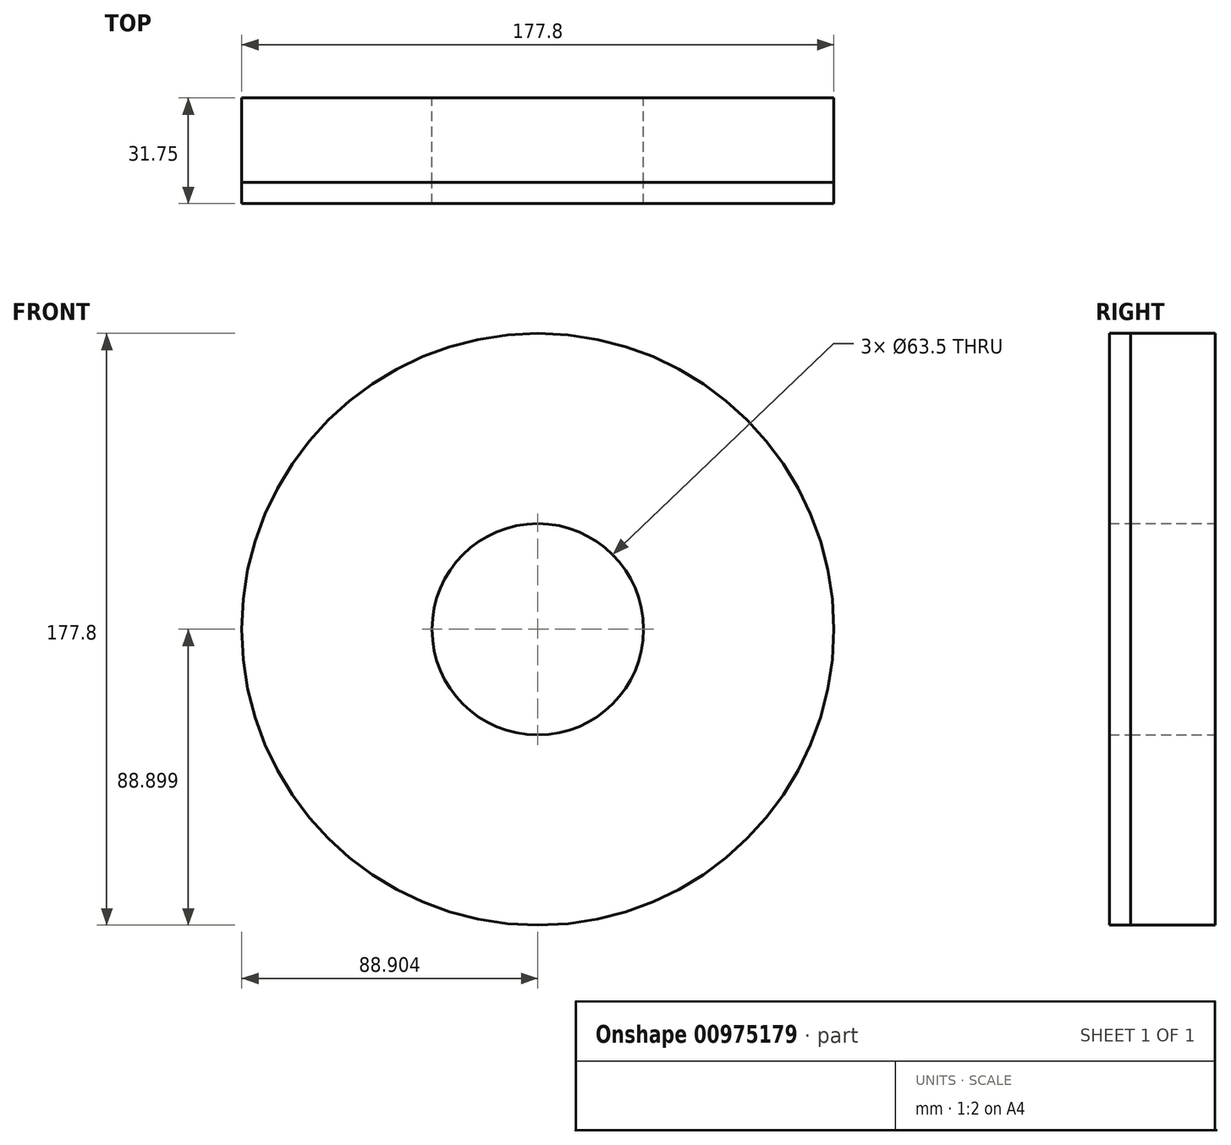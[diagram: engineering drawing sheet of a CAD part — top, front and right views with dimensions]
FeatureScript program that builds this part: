
annotation { "Feature Type Name" : "Feature", "Feature Type Description" : "" }
export const myFeature = defineFeature(function(context is Context, id is Id, definition is map)
    precondition{}
    {
        {
            var Q0;
            Q0=qCreatedBy(makeId("Front.planeOp"),FACE);
            var sketch = newSketch(context, id + "F0", { "sketchPlane" : qUnion([Q0])});
            skCircle(sketch, "E0", {"center": v(-91.18, 7.48) * mm, "radius": 88.9 * mm});
            skSolve(sketch);
        }
        {
            var Q0;
            Q0=makeQuery(id+"F0.imprint","IMPRINT",FACE,{"disambiguationData":[TD([[makeQuery(id+"F0.imprint","IMPRINT",EDGE,{"derivedFrom":sQuery(id+"F0.wireOp",EDGE,"E0")}),1.0]])]});
            extrude(context, id + "F1", {"entities" : qUnion([Q0]), "depth" : 6.35 * mm, "offsetDistance" : 25.4 * mm});
        }
        {
            var Q0;
            Q0=makeQuery(id+"F1.opExtrude","CAP_FACE",FACE,{"disambiguationData":[OSD([sQuery(id+"F0.wireOp",EDGE,"E0")])],"isStart":false});
            var sketch = newSketch(context, id + "F2", { "sketchPlane" : qUnion([Q0])});
            skLineSegment(sketch, "E1", {"start": v(-91.18, 96.38) * mm, "end": v(-91.18, -81.42) * mm});
            skCircle(sketch, "E2", {"center": v(-91.18, 7.48) * mm, "radius": 25.4 * mm});
            skCircle(sketch, "E3", {"center": v(-91.18, 7.48) * mm, "radius": 31.75 * mm});
            skSolve(sketch);
        }
        {
            var Q0;
            {var subQ0=sQuery(id+"F2.wireOp",EDGE,"E3");var subQ1=sQuery(id+"F2.wireOp",EDGE,"E1");var subQ2=makeQuery(id+"F2.imprint","INTERSECT",VERTEX,{"disambiguationData":[OD(0.0)],"derivedFrom":[subQ1,subQ0]});Q0=makeQuery(id+"F2.imprint","IMPRINT",FACE,{"disambiguationData":[TD([[makeQuery(id+"F2.imprint","IMPRINT",EDGE,{"disambiguationData":[TD([[subQ2,-1.0]])],"derivedFrom":subQ1}),-1.0]])]});}
            var Q1;
            {var subQ0=sQuery(id+"F2.wireOp",EDGE,"E3");var subQ1=sQuery(id+"F2.wireOp",EDGE,"E1");var subQ2=makeQuery(id+"F2.imprint","INTERSECT",VERTEX,{"disambiguationData":[OD(0.0)],"derivedFrom":[subQ1,subQ0]});Q1=makeQuery(id+"F2.imprint","IMPRINT",FACE,{"disambiguationData":[TD([[makeQuery(id+"F2.imprint","IMPRINT",EDGE,{"disambiguationData":[TD([[subQ2,-1.0]])],"derivedFrom":subQ1}),1.0]])]});}
            extrude(context, id + "F3", {"entities" : qUnion([Q0, Q1]), "operationType" : NewBodyOperationType.ADD, "depth" : 19.05 * mm, "offsetDistance" : 25.4 * mm});
        }
        {
            var Q0;
            Q0=makeQuery(id+"F3.opExtrude","CAP_FACE",FACE,{"disambiguationData":[OSD([sQuery(id+"F2.wireOp",EDGE,"E2"),sQuery(id+"F2.wireOp",EDGE,"E3")])],"isStart":false});
            var sketch = newSketch(context, id + "F4", { "sketchPlane" : qUnion([Q0])});
            skLineSegment(sketch, "E4", {"start": v(-91.2, 39.23) * mm, "end": v(-91.2, -24.27) * mm});
            skCircle(sketch, "E5", {"center": v(-91.18, 7.48) * mm, "radius": 88.9 * mm});
            skSolve(sketch);
        }
        {
            var Q0;
            Q0=makeQuery(id+"F4.imprint","IMPRINT",FACE,{"disambiguationData":[TD([[makeQuery(id+"F4.imprint","IMPRINT",EDGE,{"derivedFrom":sQuery(id+"F4.wireOp",EDGE,"E5")}),1.0]])]});
            extrude(context, id + "F5", {"entities" : qUnion([Q0]), "depth" : 6.35 * mm, "offsetDistance" : 25.4 * mm});
        }
        {
            var Q0;
            Q0=makeQuery(id+"F3.opExtrude","CAP_FACE",FACE,{"disambiguationData":[OSD([sQuery(id+"F2.wireOp",EDGE,"E2"),sQuery(id+"F2.wireOp",EDGE,"E3")])],"isStart":false});
            extrude(context, id + "F6", {"entities" : qUnion([Q0]), "depth" : 6.35 * mm, "offsetDistance" : 25.4 * mm});
        }
        {
            var Q0;
            Q0=makeQuery(id+"F3.boolean.opBoolean","SPLIT",FACE,{"disambiguationData":[TD([makeQuery(id+"F3.opExtrude","SWEPT_FACE",FACE,{"disambiguationData":[OSD([sQuery(id+"F2.wireOp",EDGE,"E2")])]})])],"derivedFrom":makeQuery(id+"F1.opExtrude","CAP_FACE",FACE,{"disambiguationData":[OSD([sQuery(id+"F0.wireOp",EDGE,"E0")])],"isStart":false})});
            extrude(context, id + "F7", {"entities" : qUnion([Q0]), "operationType" : NewBodyOperationType.REMOVE, "oppositeDirection" : true, "depth" : 25.4 * mm, "offsetDistance" : 25.4 * mm});
        }
    });
